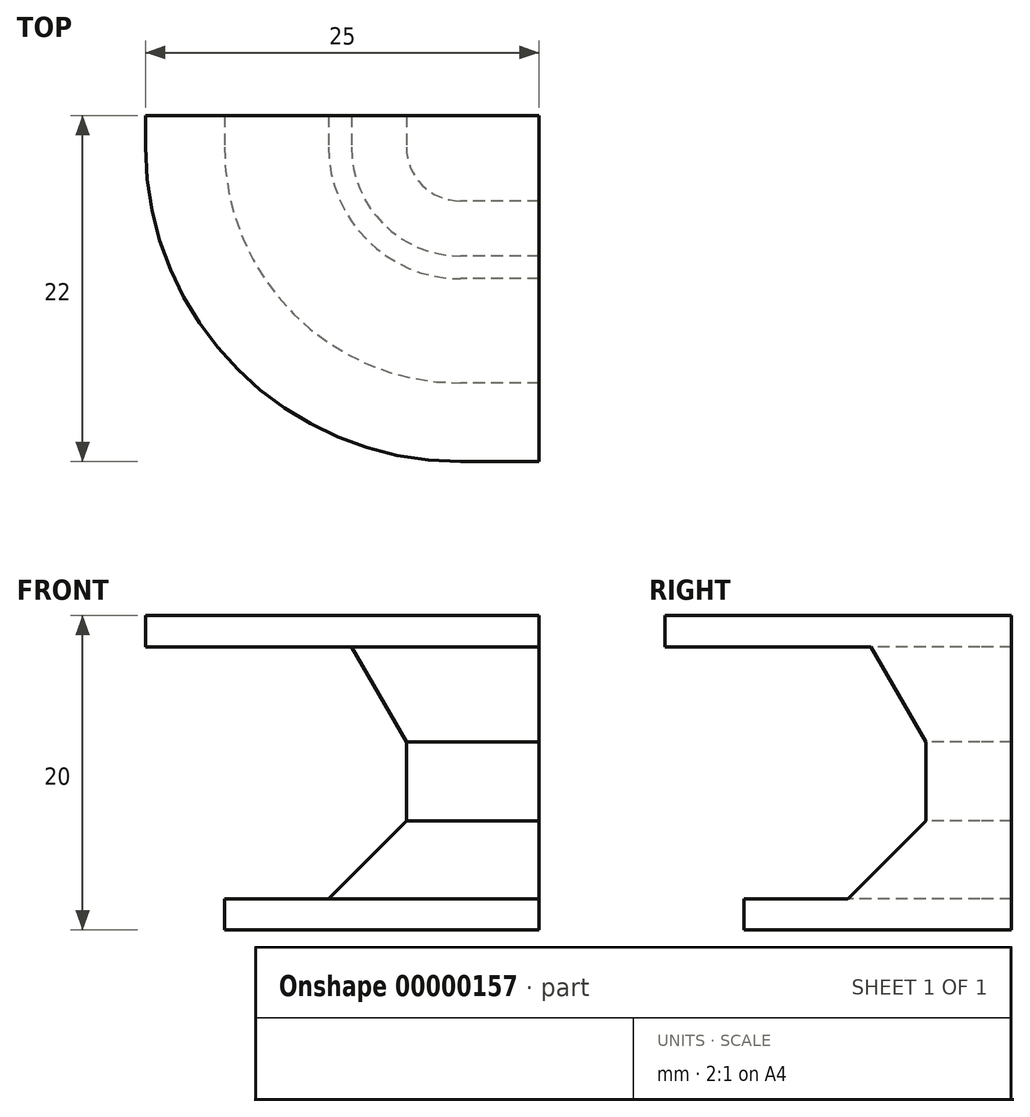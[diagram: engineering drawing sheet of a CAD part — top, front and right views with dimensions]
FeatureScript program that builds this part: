
annotation { "Feature Type Name" : "Feature", "Feature Type Description" : "" }
export const myFeature = defineFeature(function(context is Context, id is Id, definition is map)
    precondition{}
    {
        {
            var Q0;
            Q0=qCreatedBy(makeId("Right.planeOp"),FACE);
            var sketch = newSketch(context, id + "F0", { "sketchPlane" : qUnion([Q0])});
            skLineSegment(sketch, "E0", {"start": v(0, 0) * mm, "end": v(0, 20) * mm});
            skLineSegment(sketch, "E1", {"start": v(0, 20) * mm, "end": v(-20, 20) * mm});
            skLineSegment(sketch, "E2", {"start": v(-20, 20) * mm, "end": v(-20, 18) * mm});
            skLineSegment(sketch, "E3", {"start": v(-20, 18) * mm, "end": v(-6.93, 18) * mm});
            skLineSegment(sketch, "E4", {"start": v(-6.93, 18) * mm, "end": v(-3.43, 11.94) * mm});
            skLineSegment(sketch, "E5", {"start": v(-3.43, 11.94) * mm, "end": v(-3.43, 6.94) * mm});
            skLineSegment(sketch, "E6", {"start": v(-3.43, 6.94) * mm, "end": v(-8.38, 2) * mm});
            skLineSegment(sketch, "E7", {"start": v(-8.38, 2) * mm, "end": v(-15, 2) * mm});
            skLineSegment(sketch, "E8", {"start": v(-15, 2) * mm, "end": v(-15, 0) * mm});
            skLineSegment(sketch, "E9", {"start": v(-15, 0) * mm, "end": v(0, 0) * mm});
            skLineSegment(sketch, "E10", {"start": v(-3.43, 11.94) * mm, "end": v(0, 11.94) * mm, "construction": true});
            skLineSegment(sketch, "E11", {"start": v(-3.43, 6.94) * mm, "end": v(0, 6.94) * mm, "construction": true});
            skSolve(sketch);
        }
        {
            var Q0;
            Q0=makeQuery(id+"F0.imprint","IMPRINT",FACE,{"disambiguationData":[TD([[makeQuery(id+"F0.imprint","IMPRINT",EDGE,{"derivedFrom":sQuery(id+"F0.wireOp",EDGE,"E0")}),1.0]])]});
            extrude(context, id + "F1", {"entities" : qUnion([Q0]), "depth" : 5 * mm});
        }
        {
            var Q0;
            Q0=makeQuery(id+"F0.imprint","IMPRINT",FACE,{"disambiguationData":[TD([[makeQuery(id+"F0.imprint","IMPRINT",EDGE,{"derivedFrom":sQuery(id+"F0.wireOp",EDGE,"E0")}),1.0]])]});
            var Q1;
            Q1=makeQuery(id+"F1.opExtrude","CAP_EDGE",EDGE,{"disambiguationData":[OSD([sQuery(id+"F0.wireOp",EDGE,"E0")])],"isStart":true});
            revolve(context, id + "F2", {"operationType" : NewBodyOperationType.ADD, "entities" : qUnion([Q0]), "axis" : qUnion([Q1]), "revolveType" : RevolveType.ONE_DIRECTION, "oppositeDirection" : true, "angle" : 90 * degree});
        }
        {
            var Q0;
            {var subQ0=sQuery(id+"F0.wireOp",EDGE,"E0");Q0=makeQuery(id+"F2.boolean.opBoolean","MERGE",FACE,{"derivedFrom":[makeQuery(id+"F1.opExtrude","SWEPT_FACE",FACE,{"disambiguationData":[OSD([subQ0])]}),makeQuery(id+"F2.opRevolve","CAP_FACE",FACE,{"disambiguationData":[OSD([subQ0,sQuery(id+"F0.wireOp",EDGE,"E1"),sQuery(id+"F0.wireOp",EDGE,"E2"),sQuery(id+"F0.wireOp",EDGE,"E3"),sQuery(id+"F0.wireOp",EDGE,"E4"),sQuery(id+"F0.wireOp",EDGE,"E5"),sQuery(id+"F0.wireOp",EDGE,"E6"),sQuery(id+"F0.wireOp",EDGE,"E7"),sQuery(id+"F0.wireOp",EDGE,"E8"),sQuery(id+"F0.wireOp",EDGE,"E9")])],"isStart":false})]});}
            extrude(context, id + "F3", {"entities" : qUnion([Q0]), "operationType" : NewBodyOperationType.ADD, "depth" : 2 * mm});
        }
    });
